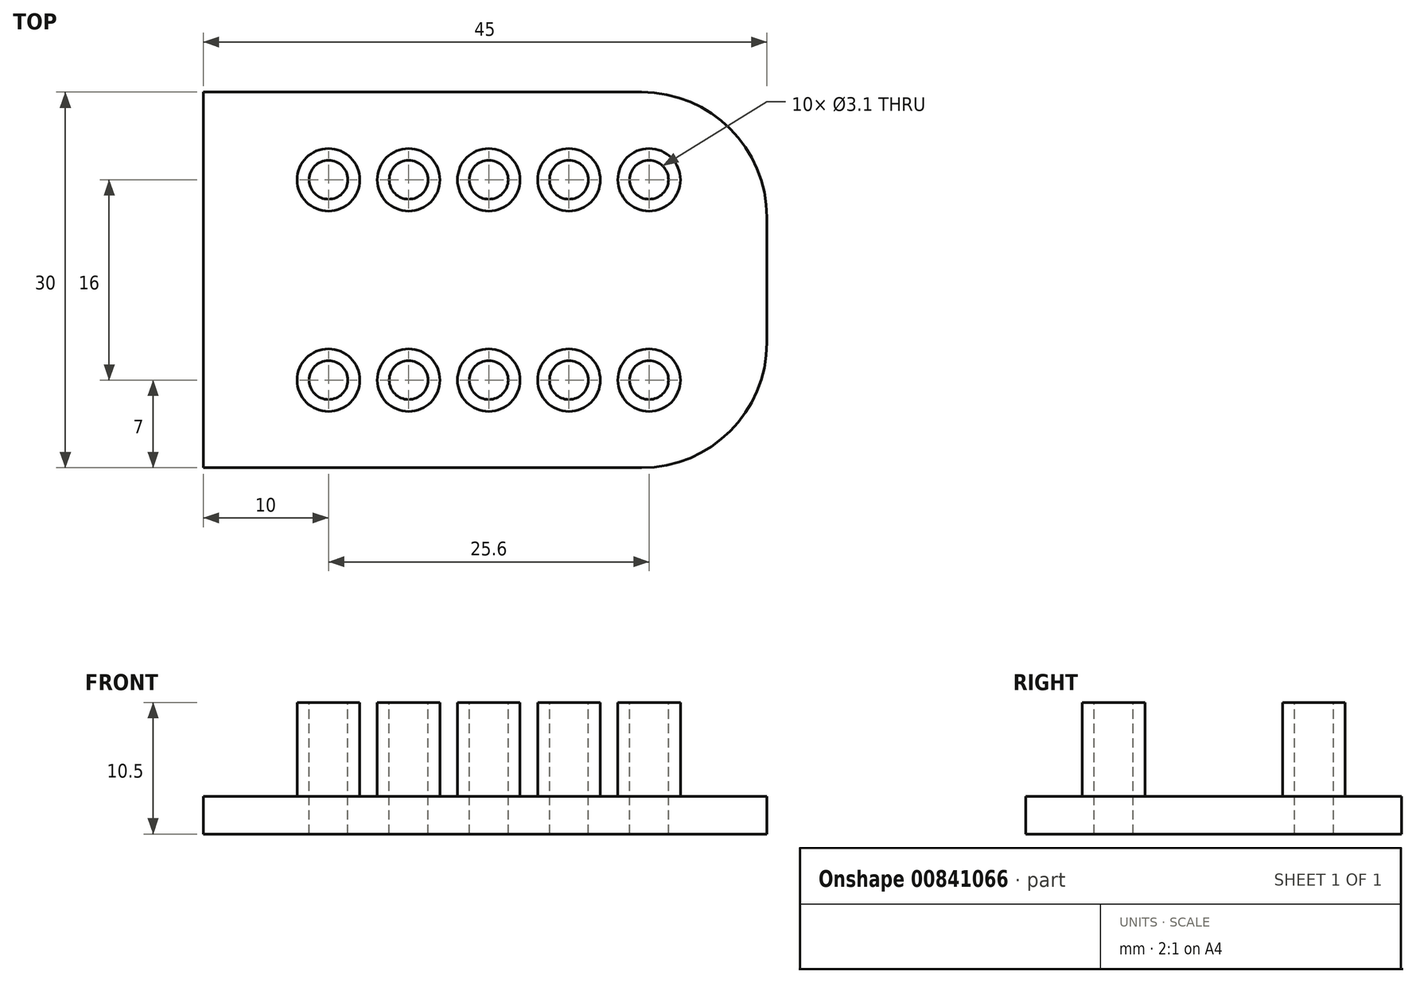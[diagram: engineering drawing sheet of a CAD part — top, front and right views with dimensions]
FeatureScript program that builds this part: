
annotation { "Feature Type Name" : "Feature", "Feature Type Description" : "" }
export const myFeature = defineFeature(function(context is Context, id is Id, definition is map)
    precondition{}
    {
        {
            var Q0;
            Q0=qCreatedBy(makeId("Top.planeOp"),FACE);
            var sketch = newSketch(context, id + "F0", { "sketchPlane" : qUnion([Q0])});
            skLineSegment(sketch, "E0.bottom", {"start": v(0, 0) * mm, "end": v(45, 0) * mm});
            skLineSegment(sketch, "E0.top", {"start": v(0, 30) * mm, "end": v(45, 30) * mm});
            skLineSegment(sketch, "E0.left", {"start": v(0, 0) * mm, "end": v(0, 30) * mm});
            skLineSegment(sketch, "E0.right", {"start": v(45, 0) * mm, "end": v(45, 30) * mm});
            skCircle(sketch, "E1", {"center": v(10, 7) * mm, "radius": 1.55 * mm});
            skCircle(sketch, "E2.0.1.0", {"center": v(10, 23) * mm, "radius": 1.55 * mm});
            skCircle(sketch, "E2.1.0.0", {"center": v(16.4, 7) * mm, "radius": 1.55 * mm});
            skCircle(sketch, "E2.1.1.0", {"center": v(16.4, 23) * mm, "radius": 1.55 * mm});
            skCircle(sketch, "E2.2.0.0", {"center": v(22.8, 7) * mm, "radius": 1.55 * mm});
            skCircle(sketch, "E2.2.1.0", {"center": v(22.8, 23) * mm, "radius": 1.55 * mm});
            skCircle(sketch, "E2.3.0.0", {"center": v(29.2, 7) * mm, "radius": 1.55 * mm});
            skCircle(sketch, "E2.3.1.0", {"center": v(29.2, 23) * mm, "radius": 1.55 * mm});
            skCircle(sketch, "E2.4.0.0", {"center": v(35.6, 7) * mm, "radius": 1.55 * mm});
            skCircle(sketch, "E2.4.1.0", {"center": v(35.6, 23) * mm, "radius": 1.55 * mm});
            skLineSegment(sketch, "E2.direction1", {"start": v(10, 7) * mm, "end": v(16.4, 7) * mm, "construction": true});
            skLineSegment(sketch, "E2.direction2", {"start": v(10, 7) * mm, "end": v(10, 23) * mm, "construction": true});
            skCircle(sketch, "E3", {"center": v(35.6, 23) * mm, "radius": 2.5 * mm});
            skCircle(sketch, "E4", {"center": v(29.2, 23) * mm, "radius": 2.5 * mm});
            skCircle(sketch, "E5", {"center": v(22.8, 23) * mm, "radius": 2.5 * mm});
            skCircle(sketch, "E6", {"center": v(16.4, 23) * mm, "radius": 2.5 * mm});
            skCircle(sketch, "E7", {"center": v(10, 23) * mm, "radius": 2.5 * mm});
            skCircle(sketch, "E8", {"center": v(35.6, 7) * mm, "radius": 2.5 * mm});
            skCircle(sketch, "E9", {"center": v(29.2, 7) * mm, "radius": 2.5 * mm});
            skCircle(sketch, "E10", {"center": v(22.8, 7) * mm, "radius": 2.5 * mm});
            skCircle(sketch, "E11", {"center": v(16.4, 7) * mm, "radius": 2.5 * mm});
            skCircle(sketch, "E12", {"center": v(10, 7) * mm, "radius": 2.5 * mm});
            skSolve(sketch);
        }
        {
            var Q0;
            Q0=makeQuery(id+"F0.imprint","IMPRINT",FACE,{"disambiguationData":[TD([[makeQuery(id+"F0.imprint","IMPRINT",EDGE,{"derivedFrom":sQuery(id+"F0.wireOp",EDGE,"E0.bottom")}),1.0]])]});
            var Q1;
            Q1=makeQuery(id+"F0.imprint","IMPRINT",FACE,{"disambiguationData":[TD([[makeQuery(id+"F0.imprint","IMPRINT",EDGE,{"derivedFrom":sQuery(id+"F0.wireOp",EDGE,"E2.4.1.0")}),-1.0]])]});
            var Q2;
            Q2=makeQuery(id+"F0.imprint","IMPRINT",FACE,{"disambiguationData":[TD([[makeQuery(id+"F0.imprint","IMPRINT",EDGE,{"derivedFrom":sQuery(id+"F0.wireOp",EDGE,"E2.3.1.0")}),-1.0]])]});
            var Q3;
            Q3=makeQuery(id+"F0.imprint","IMPRINT",FACE,{"disambiguationData":[TD([[makeQuery(id+"F0.imprint","IMPRINT",EDGE,{"derivedFrom":sQuery(id+"F0.wireOp",EDGE,"E2.2.1.0")}),-1.0]])]});
            var Q4;
            Q4=makeQuery(id+"F0.imprint","IMPRINT",FACE,{"disambiguationData":[TD([[makeQuery(id+"F0.imprint","IMPRINT",EDGE,{"derivedFrom":sQuery(id+"F0.wireOp",EDGE,"E2.1.1.0")}),-1.0]])]});
            var Q5;
            Q5=makeQuery(id+"F0.imprint","IMPRINT",FACE,{"disambiguationData":[TD([[makeQuery(id+"F0.imprint","IMPRINT",EDGE,{"derivedFrom":sQuery(id+"F0.wireOp",EDGE,"E2.0.1.0")}),-1.0]])]});
            var Q6;
            Q6=makeQuery(id+"F0.imprint","IMPRINT",FACE,{"disambiguationData":[TD([[makeQuery(id+"F0.imprint","IMPRINT",EDGE,{"derivedFrom":sQuery(id+"F0.wireOp",EDGE,"E1")}),-1.0]])]});
            var Q7;
            Q7=makeQuery(id+"F0.imprint","IMPRINT",FACE,{"disambiguationData":[TD([[makeQuery(id+"F0.imprint","IMPRINT",EDGE,{"derivedFrom":sQuery(id+"F0.wireOp",EDGE,"E2.1.0.0")}),-1.0]])]});
            var Q8;
            Q8=makeQuery(id+"F0.imprint","IMPRINT",FACE,{"disambiguationData":[TD([[makeQuery(id+"F0.imprint","IMPRINT",EDGE,{"derivedFrom":sQuery(id+"F0.wireOp",EDGE,"E2.2.0.0")}),-1.0]])]});
            var Q9;
            Q9=makeQuery(id+"F0.imprint","IMPRINT",FACE,{"disambiguationData":[TD([[makeQuery(id+"F0.imprint","IMPRINT",EDGE,{"derivedFrom":sQuery(id+"F0.wireOp",EDGE,"E2.3.0.0")}),-1.0]])]});
            var Q10;
            Q10=makeQuery(id+"F0.imprint","IMPRINT",FACE,{"disambiguationData":[TD([[makeQuery(id+"F0.imprint","IMPRINT",EDGE,{"derivedFrom":sQuery(id+"F0.wireOp",EDGE,"E2.4.0.0")}),-1.0]])]});
            extrude(context, id + "F1", {"entities" : qUnion([Q0, Q1, Q2, Q3, Q4, Q5, Q6, Q7, Q8, Q9, Q10]), "depth" : 3 * mm, "offsetDistance" : 25 * mm});
        }
        {
            var Q0;
            Q0=makeQuery(id+"F0.imprint","IMPRINT",FACE,{"disambiguationData":[TD([[makeQuery(id+"F0.imprint","IMPRINT",EDGE,{"derivedFrom":sQuery(id+"F0.wireOp",EDGE,"E2.4.1.0")}),-1.0]])]});
            var Q1;
            Q1=makeQuery(id+"F0.imprint","IMPRINT",FACE,{"disambiguationData":[TD([[makeQuery(id+"F0.imprint","IMPRINT",EDGE,{"derivedFrom":sQuery(id+"F0.wireOp",EDGE,"E2.3.1.0")}),-1.0]])]});
            var Q2;
            Q2=makeQuery(id+"F0.imprint","IMPRINT",FACE,{"disambiguationData":[TD([[makeQuery(id+"F0.imprint","IMPRINT",EDGE,{"derivedFrom":sQuery(id+"F0.wireOp",EDGE,"E2.2.1.0")}),-1.0]])]});
            var Q3;
            Q3=makeQuery(id+"F0.imprint","IMPRINT",FACE,{"disambiguationData":[TD([[makeQuery(id+"F0.imprint","IMPRINT",EDGE,{"derivedFrom":sQuery(id+"F0.wireOp",EDGE,"E2.1.1.0")}),-1.0]])]});
            var Q4;
            Q4=makeQuery(id+"F0.imprint","IMPRINT",FACE,{"disambiguationData":[TD([[makeQuery(id+"F0.imprint","IMPRINT",EDGE,{"derivedFrom":sQuery(id+"F0.wireOp",EDGE,"E2.0.1.0")}),-1.0]])]});
            var Q5;
            Q5=makeQuery(id+"F0.imprint","IMPRINT",FACE,{"disambiguationData":[TD([[makeQuery(id+"F0.imprint","IMPRINT",EDGE,{"derivedFrom":sQuery(id+"F0.wireOp",EDGE,"E1")}),-1.0]])]});
            var Q6;
            Q6=makeQuery(id+"F0.imprint","IMPRINT",FACE,{"disambiguationData":[TD([[makeQuery(id+"F0.imprint","IMPRINT",EDGE,{"derivedFrom":sQuery(id+"F0.wireOp",EDGE,"E2.1.0.0")}),-1.0]])]});
            var Q7;
            Q7=makeQuery(id+"F0.imprint","IMPRINT",FACE,{"disambiguationData":[TD([[makeQuery(id+"F0.imprint","IMPRINT",EDGE,{"derivedFrom":sQuery(id+"F0.wireOp",EDGE,"E2.2.0.0")}),-1.0]])]});
            var Q8;
            Q8=makeQuery(id+"F0.imprint","IMPRINT",FACE,{"disambiguationData":[TD([[makeQuery(id+"F0.imprint","IMPRINT",EDGE,{"derivedFrom":sQuery(id+"F0.wireOp",EDGE,"E2.3.0.0")}),-1.0]])]});
            var Q9;
            Q9=makeQuery(id+"F0.imprint","IMPRINT",FACE,{"disambiguationData":[TD([[makeQuery(id+"F0.imprint","IMPRINT",EDGE,{"derivedFrom":sQuery(id+"F0.wireOp",EDGE,"E2.4.0.0")}),-1.0]])]});
            extrude(context, id + "F2", {"entities" : qUnion([Q0, Q1, Q2, Q3, Q4, Q5, Q6, Q7, Q8, Q9]), "operationType" : NewBodyOperationType.ADD, "oppositeDirection" : true, "depth" : 7.5 * mm, "offsetDistance" : 25 * mm});
        }
        {
            var Q0;
            Q0=makeQuery(id+"F1.opExtrude","SWEPT_EDGE",EDGE,{"disambiguationData":[OSD([sQuery(id+"F0.wireOp",EDGE,"E0.top"),sQuery(id+"F0.wireOp",EDGE,"E0.right")])]});
            var Q1;
            Q1=makeQuery(id+"F1.opExtrude","SWEPT_EDGE",EDGE,{"disambiguationData":[OSD([sQuery(id+"F0.wireOp",EDGE,"E0.bottom"),sQuery(id+"F0.wireOp",EDGE,"E0.right")])]});
            fillet(context, id + "F3", {"entities" : qUnion([Q0, Q1]), "radius" : 10 * mm, "tangentPropagation" : true, "allowEdgeOverflow" : false});
        }
        {
            var Q0;
            Q0=makeQuery(id+"F1.opExtrude","SWEPT_BODY",BODY,{"disambiguationData":[OSD([sQuery(id+"F0.wireOp",EDGE,"E0.bottom"),sQuery(id+"F0.wireOp",EDGE,"E0.top"),sQuery(id+"F0.wireOp",EDGE,"E0.left"),sQuery(id+"F0.wireOp",EDGE,"E0.right"),sQuery(id+"F0.wireOp",EDGE,"E1"),sQuery(id+"F0.wireOp",EDGE,"E2.0.1.0"),sQuery(id+"F0.wireOp",EDGE,"E2.1.0.0"),sQuery(id+"F0.wireOp",EDGE,"E2.1.1.0"),sQuery(id+"F0.wireOp",EDGE,"E2.2.0.0"),sQuery(id+"F0.wireOp",EDGE,"E2.2.1.0"),sQuery(id+"F0.wireOp",EDGE,"E2.3.0.0"),sQuery(id+"F0.wireOp",EDGE,"E2.3.1.0"),sQuery(id+"F0.wireOp",EDGE,"E2.4.0.0"),sQuery(id+"F0.wireOp",EDGE,"E2.4.1.0")])]});
            var Q1;
            Q1=sQuery(id+"F0.wireOp",EDGE,"E0.bottom");
            var Q2;
            Q2=sQuery(id+"F0.wireOp",EDGE,"E0.bottom");
            transform(context, id + "F4", {"entities" : qUnion([Q0]), "transformType" : TransformType.ROTATION, "transformAxis" : qUnion([Q2]), "angle" : 180 * degree, "makeCopy" : false});
        }
    });
